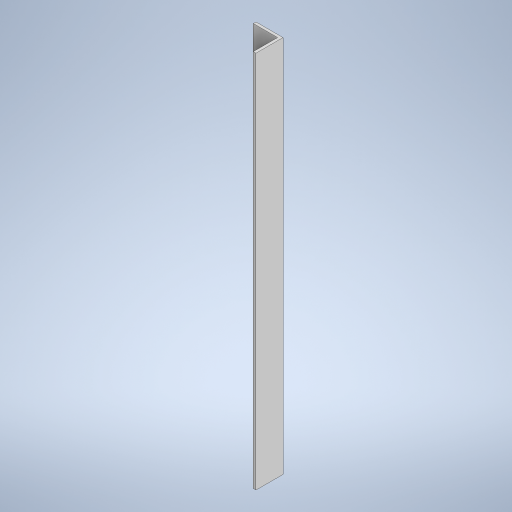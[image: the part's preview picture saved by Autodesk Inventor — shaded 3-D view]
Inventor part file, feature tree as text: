
AUTODESK INVENTOR PART (.ipt)
format: ipt  version: 2024 (Build 280153000, 153)  size: 235,520 bytes
history: native  units: mm
features: extrude x1, sketch x1
ambient origin geometry x8: Origin, YZ Plane, XZ Plane, XY Plane, X Axis, Y Axis, Z Axis, Center Point
bodies: Solid1 (feature_tree)
feature tree (2):
  extrude  "Extrusion1"  Depth=50.0mm
  sketch  "Sketch1"  dims[d0=50.0mm d1=50.0mm d3=5.0mm d4=5.0mm d5=700.0mm d6=0.0mm]
